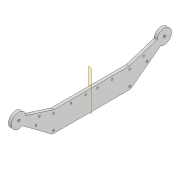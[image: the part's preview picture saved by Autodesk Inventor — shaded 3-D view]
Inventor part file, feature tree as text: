
AUTODESK INVENTOR PART (.ipt)
format: ipt  version: 2022 (Build 260153000, 153)  size: 237,568 bytes
history: native  units: mm
features: extrude x1, sketch x1
ambient origin geometry x8: Origin, YZ Plane, XZ Plane, XY Plane, X Axis, Y Axis, Z Axis, Center Point
bodies: Solid1 (feature_tree)
feature tree (2):
  extrude  "Extrusion1"  Depth=10.0mm
  sketch  "Sketch1"  dims[d2=3.9mm d4=3.9mm d6=5.0mm d7=0.0mm d25=3.0mm d28=3.0mm d43=59.0mm d44=65.0mm d45=65.0mm d47=59.0mm d48=10.0mm d49=10.0mm d50=10.0mm d52=14.0mm d53=3.0mm d54=3.0mm d55=4.0mm d56=4.0mm d57=25.0mm d58=25.0mm d59=10.0mm d60=10.0mm d61=10.0mm d62=3.0mm d63=3.0mm d64=3.0mm d65=3.0mm d66=3.0mm d67=10.0mm d68=25.0mm d69=3.0mm d70=3.0mm d71=10.0mm d72=25.0mm d73=25.0mm d74=25.0mm d76=3.0mm d78=3.0mm d79=3.0mm d80=3.0mm d81=6.0mm d82=6.0mm d83=2.0mm]
